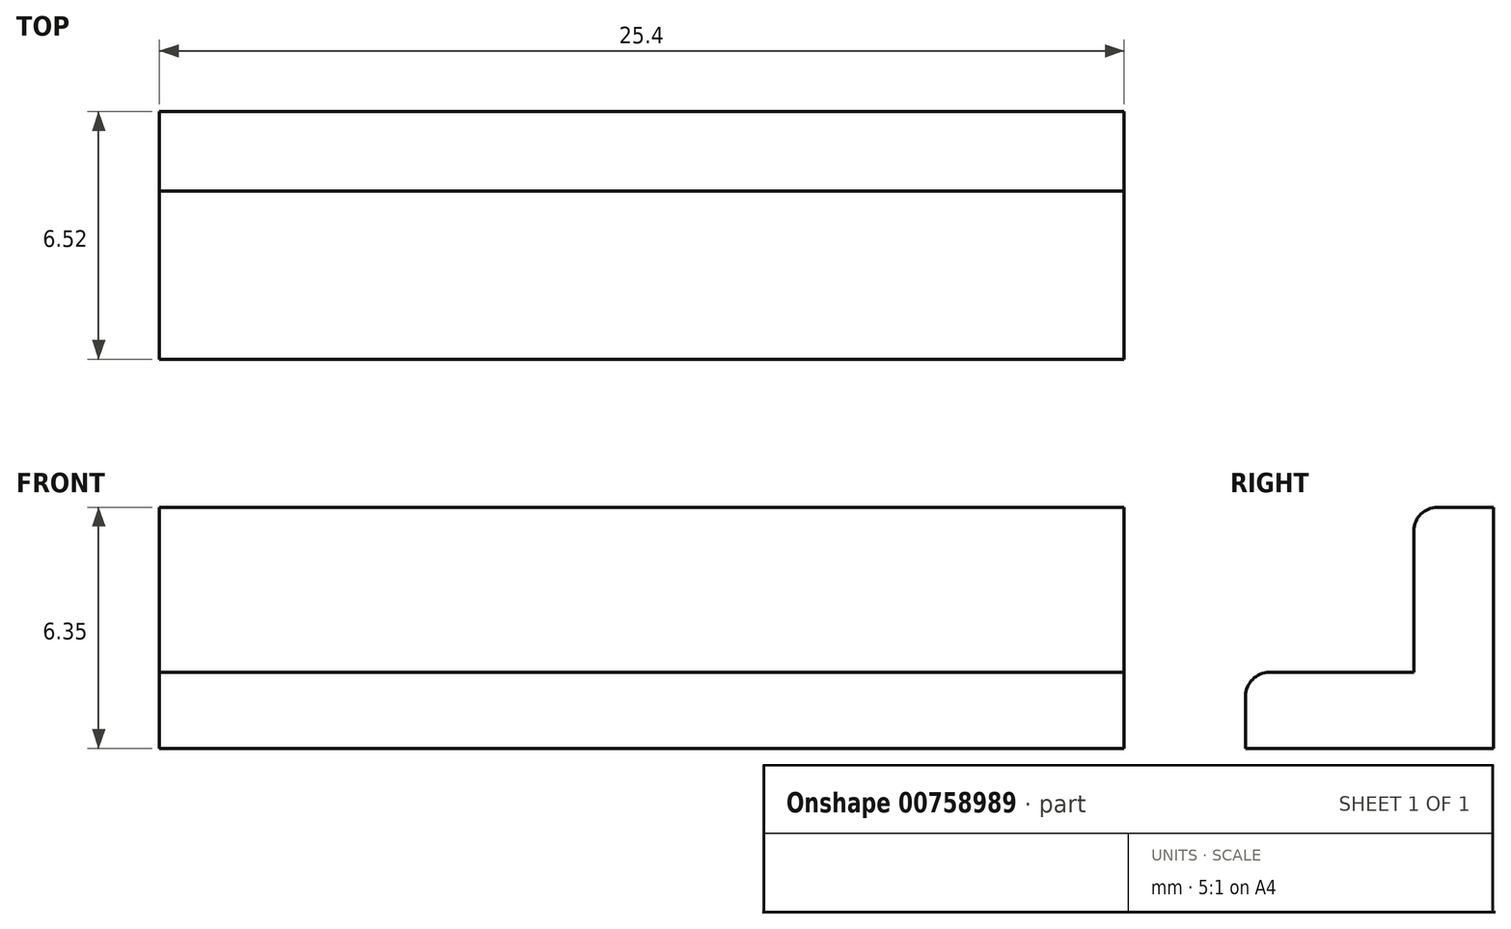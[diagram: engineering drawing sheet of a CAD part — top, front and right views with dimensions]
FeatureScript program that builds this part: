
annotation { "Feature Type Name" : "Feature", "Feature Type Description" : "" }
export const myFeature = defineFeature(function(context is Context, id is Id, definition is map)
    precondition{}
    {
        {
            var Q0;
            Q0=qCreatedBy(makeId("Right.planeOp"),FACE);
            var sketch = newSketch(context, id + "F0", { "sketchPlane" : qUnion([Q0])});
            skLineSegment(sketch, "E0", {"start": v(-10.66, 0) * mm, "end": v(-4.14, 0) * mm});
            skLineSegment(sketch, "E1", {"start": v(-4.14, 0) * mm, "end": v(-4.14, 6.35) * mm});
            skLineSegment(sketch, "E2", {"start": v(-4.14, 6.35) * mm, "end": v(-5.6, 6.35) * mm});
            skLineSegment(sketch, "E3", {"start": v(-6.23, 5.72) * mm, "end": v(-6.23, 2) * mm});
            skLineSegment(sketch, "E4", {"start": v(-6.23, 2) * mm, "end": v(-10.04, 2) * mm});
            skLineSegment(sketch, "E5", {"start": v(-10.66, 1.38) * mm, "end": v(-10.66, 0) * mm});
            skPoint(sketch, "E6.visualSharp", {"position": v(-10.66, 2) * mm});
            skArc(sketch, "E6.filletArc", {"start": v(-10.04, 2) * mm, "mid": v(-10.48, 1.82) * mm, "end": v(-10.66, 1.38) * mm});
            skPoint(sketch, "E7.visualSharp", {"position": v(-6.23, 6.35) * mm});
            skArc(sketch, "E7.filletArc", {"start": v(-5.6, 6.35) * mm, "mid": v(-6.05, 6.17) * mm, "end": v(-6.23, 5.72) * mm});
            skSolve(sketch);
        }
        {
            var Q0;
            Q0=makeQuery(id+"F0.imprint","IMPRINT",FACE,{"disambiguationData":[TD([[makeQuery(id+"F0.imprint","IMPRINT",EDGE,{"derivedFrom":sQuery(id+"F0.wireOp",EDGE,"E0")}),1.0]])]});
            extrude(context, id + "F1", {"entities" : qUnion([Q0]), "depth" : 25.4 * mm, "offsetDistance" : 25.4 * mm});
        }
    });
